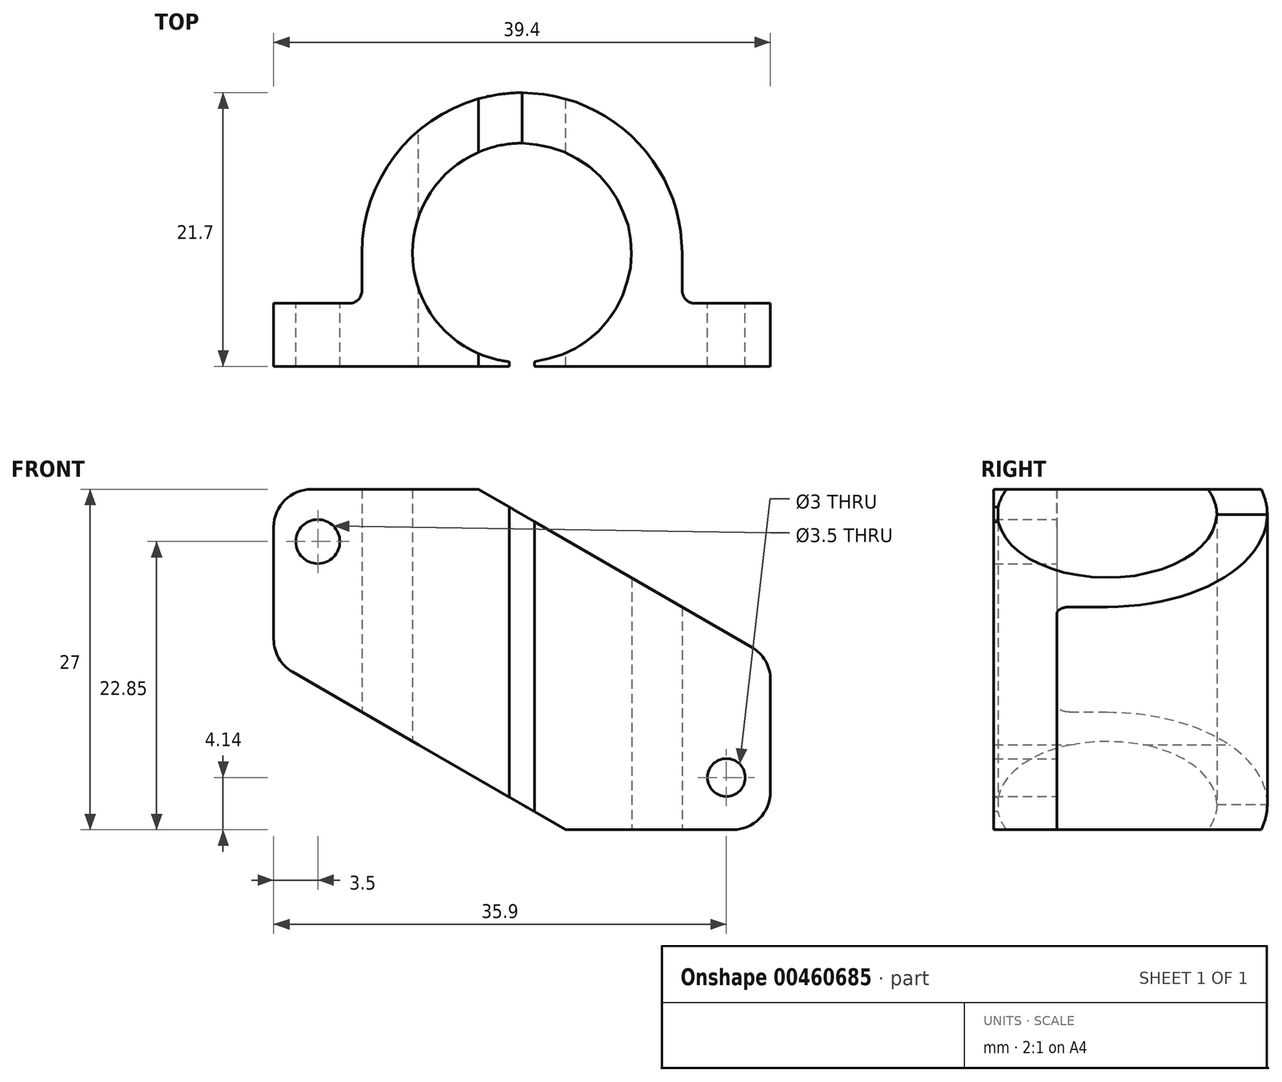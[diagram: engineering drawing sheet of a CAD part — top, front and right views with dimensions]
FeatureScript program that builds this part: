
annotation { "Feature Type Name" : "Feature", "Feature Type Description" : "" }
export const myFeature = defineFeature(function(context is Context, id is Id, definition is map)
    precondition{}
    {
        {
            var Q0;
            Q0=qCreatedBy(makeId("Top.planeOp"),FACE);
            var sketch = newSketch(context, id + "F0", { "sketchPlane" : qUnion([Q0])});
            skCircle(sketch, "E0", {"center": v(0, 0) * mm, "radius": 8.7 * mm});
            skCircle(sketch, "E1", {"center": v(0, 0) * mm, "radius": 12.7 * mm});
            skLineSegment(sketch, "E2.bottom", {"start": v(-12.7, 0) * mm, "end": v(12.7, 0) * mm});
            skLineSegment(sketch, "E2.top", {"start": v(-12.7, -9) * mm, "end": v(12.7, -9) * mm});
            skLineSegment(sketch, "E2.left", {"start": v(-12.7, 0) * mm, "end": v(-12.7, -9) * mm});
            skLineSegment(sketch, "E2.right", {"start": v(12.7, 0) * mm, "end": v(12.7, -9) * mm});
            skLineSegment(sketch, "E3.bottom", {"start": v(-19.7, -9) * mm, "end": v(19.7, -9) * mm});
            skLineSegment(sketch, "E3.top", {"start": v(-19.7, -4) * mm, "end": v(19.7, -4) * mm});
            skLineSegment(sketch, "E3.left", {"start": v(-19.7, -9) * mm, "end": v(-19.7, -4) * mm});
            skLineSegment(sketch, "E3.right", {"start": v(19.7, -9) * mm, "end": v(19.7, -4) * mm});
            skLineSegment(sketch, "E4.bottom", {"start": v(-1, -9) * mm, "end": v(1, -9) * mm});
            skLineSegment(sketch, "E4.top", {"start": v(-1, -4) * mm, "end": v(1, -4) * mm});
            skLineSegment(sketch, "E4.left", {"start": v(-1, -9) * mm, "end": v(-1, -4) * mm});
            skLineSegment(sketch, "E4.right", {"start": v(1, -9) * mm, "end": v(1, -4) * mm});
            skSolve(sketch);
        }
        {
            var Q0;
            {var subQ5=sQuery(id+"F0.wireOp",EDGE,"E3.left");Q0=makeQuery(id+"F0.imprint","IMPRINT",FACE,{"disambiguationData":[TD([[makeQuery(id+"F0.imprint","IMPRINT",EDGE,{"derivedFrom":subQ5}),-1.0]])]});}
            var Q1;
            {var subQ5=sQuery(id+"F0.wireOp",EDGE,"E3.right");Q1=makeQuery(id+"F0.imprint","IMPRINT",FACE,{"disambiguationData":[TD([[makeQuery(id+"F0.imprint","IMPRINT",EDGE,{"derivedFrom":subQ5}),1.0]])]});}
            var Q2;
            {var subQ0=sQuery(id+"F0.wireOp",EDGE,"E2.left");var subQ3=sQuery(id+"F0.wireOp",EDGE,"E3.top");var subQ5=makeQuery(id+"F0.imprint","INTERSECT",VERTEX,{"derivedFrom":[subQ0,subQ3]});Q2=makeQuery(id+"F0.imprint","IMPRINT",FACE,{"disambiguationData":[TD([[makeQuery(id+"F0.imprint","IMPRINT",EDGE,{"disambiguationData":[TD([[subQ5,-1.0]])],"derivedFrom":subQ3}),1.0]])]});}
            var Q3;
            {var subQ0=sQuery(id+"F0.wireOp",EDGE,"E2.right");var subQ3=sQuery(id+"F0.wireOp",EDGE,"E3.top");var subQ5=makeQuery(id+"F0.imprint","INTERSECT",VERTEX,{"derivedFrom":[subQ0,subQ3]});Q3=makeQuery(id+"F0.imprint","IMPRINT",FACE,{"disambiguationData":[TD([[makeQuery(id+"F0.imprint","IMPRINT",EDGE,{"disambiguationData":[TD([[subQ5,1.0]])],"derivedFrom":subQ3}),1.0]])]});}
            var Q4;
            {var subQ0=sQuery(id+"F0.wireOp",EDGE,"E2.bottom");var subQ1=sQuery(id+"F0.wireOp",EDGE,"E0");var subQ2=makeQuery(id+"F0.imprint","INTERSECT",VERTEX,{"disambiguationData":[OD(0.0)],"derivedFrom":[subQ1,subQ0]});Q4=makeQuery(id+"F0.imprint","IMPRINT",FACE,{"disambiguationData":[TD([[makeQuery(id+"F0.imprint","IMPRINT",EDGE,{"disambiguationData":[TD([[subQ2,1.0]])],"derivedFrom":subQ1}),-1.0]])]});}
            var Q5;
            {var subQ0=sQuery(id+"F0.wireOp",EDGE,"E2.top");var subQ1=sQuery(id+"F0.wireOp",EDGE,"E1");var subQ2=makeQuery(id+"F0.imprint","INTERSECT",VERTEX,{"disambiguationData":[OD(0.0)],"derivedFrom":[subQ1,subQ0]});Q5=makeQuery(id+"F0.imprint","IMPRINT",FACE,{"disambiguationData":[TD([[makeQuery(id+"F0.imprint","IMPRINT",EDGE,{"disambiguationData":[TD([[subQ2,1.0]])],"derivedFrom":subQ1}),-1.0]])]});}
            var Q6;
            {var subQ0=sQuery(id+"F0.wireOp",EDGE,"E2.top");var subQ1=sQuery(id+"F0.wireOp",EDGE,"E1");var subQ2=makeQuery(id+"F0.imprint","INTERSECT",VERTEX,{"disambiguationData":[OD(1.0)],"derivedFrom":[subQ1,subQ0]});Q6=makeQuery(id+"F0.imprint","IMPRINT",FACE,{"disambiguationData":[TD([[makeQuery(id+"F0.imprint","IMPRINT",EDGE,{"disambiguationData":[TD([[subQ2,-1.0]])],"derivedFrom":subQ1}),-1.0]])]});}
            var Q7;
            {var subQ0=sQuery(id+"F0.wireOp",EDGE,"E2.bottom");var subQ1=sQuery(id+"F0.wireOp",EDGE,"E0");var subQ2=makeQuery(id+"F0.imprint","INTERSECT",VERTEX,{"disambiguationData":[OD(0.0)],"derivedFrom":[subQ1,subQ0]});Q7=makeQuery(id+"F0.imprint","IMPRINT",FACE,{"disambiguationData":[TD([[makeQuery(id+"F0.imprint","IMPRINT",EDGE,{"disambiguationData":[TD([[subQ2,-1.0]])],"derivedFrom":subQ1}),-1.0]])]});}
            var Q8;
            {var subQ0=sQuery(id+"F0.wireOp",EDGE,"E2.bottom");var subQ1=sQuery(id+"F0.wireOp",EDGE,"E0");var subQ2=makeQuery(id+"F0.imprint","INTERSECT",VERTEX,{"disambiguationData":[OD(1.0)],"derivedFrom":[subQ1,subQ0]});Q8=makeQuery(id+"F0.imprint","IMPRINT",FACE,{"disambiguationData":[TD([[makeQuery(id+"F0.imprint","IMPRINT",EDGE,{"disambiguationData":[TD([[subQ2,1.0]])],"derivedFrom":subQ1}),-1.0]])]});}
            var Q9;
            {var subQ1=sQuery(id+"F0.wireOp",EDGE,"E0");var subQ7=sQuery(id+"F0.wireOp",EDGE,"E4.left");var subQ9=makeQuery(id+"F0.imprint","INTERSECT",VERTEX,{"derivedFrom":[subQ1,subQ7]});Q9=makeQuery(id+"F0.imprint","IMPRINT",FACE,{"disambiguationData":[TD([[makeQuery(id+"F0.imprint","IMPRINT",EDGE,{"disambiguationData":[TD([[subQ9,1.0]])],"derivedFrom":subQ1}),-1.0]])]});}
            var Q10;
            {var subQ1=sQuery(id+"F0.wireOp",EDGE,"E0");var subQ5=sQuery(id+"F0.wireOp",EDGE,"E4.right");var subQ9=makeQuery(id+"F0.imprint","INTERSECT",VERTEX,{"derivedFrom":[subQ1,subQ5]});Q10=makeQuery(id+"F0.imprint","IMPRINT",FACE,{"disambiguationData":[TD([[makeQuery(id+"F0.imprint","IMPRINT",EDGE,{"disambiguationData":[TD([[subQ9,-1.0]])],"derivedFrom":subQ1}),-1.0]])]});}
            extrude(context, id + "F1", {"entities" : qUnion([Q0, Q1, Q2, Q3, Q4, Q5, Q6, Q7, Q8, Q9, Q10]), "depth" : 25 * mm, "offsetDistance" : 25 * mm, "hasSecondDirection" : true, "secondDirectionOppositeDirection" : true, "secondDirectionDepth" : 2 * mm});
        }
        {
            var Q0;
            Q0=qCreatedBy(makeId("Front.planeOp"),FACE);
            var sketch = newSketch(context, id + "F2", { "sketchPlane" : qUnion([Q0])});
            skLineSegment(sketch, "E5", {"start": v(0, 0) * mm, "end": v(-8.2, 0) * mm});
            skLineSegment(sketch, "E6", {"start": v(-8.2, 0) * mm, "end": v(-8.2, 4.74) * mm});
            skLineSegment(sketch, "E7", {"start": v(-8.2, 4.74) * mm, "end": v(0, 0) * mm});
            skLineSegment(sketch, "E8", {"start": v(-21.54, 12.43) * mm, "end": v(-21.54, -2) * mm});
            skLineSegment(sketch, "E9", {"start": v(-21.54, -2) * mm, "end": v(3.46, -2) * mm});
            skLineSegment(sketch, "E10", {"start": v(3.46, -2) * mm, "end": v(-21.54, 12.43) * mm});
            skSolve(sketch);
        }
        {
            var Q0;
            Q0=qCreatedBy(makeId("Front.planeOp"),FACE);
            var sketch = newSketch(context, id + "F3", { "sketchPlane" : qUnion([Q0])});
            skLineSegment(sketch, "E11", {"start": v(0, 23) * mm, "end": v(39.84, 0) * mm});
            skLineSegment(sketch, "E12", {"start": v(39.84, 0) * mm, "end": v(39.84, 23) * mm});
            skLineSegment(sketch, "E13", {"start": v(39.84, 23) * mm, "end": v(0, 23) * mm});
            skLineSegment(sketch, "E14", {"start": v(29, 6.26) * mm, "end": v(29, 25) * mm});
            skLineSegment(sketch, "E15", {"start": v(29, 25) * mm, "end": v(-3.46, 25) * mm});
            skLineSegment(sketch, "E16", {"start": v(-3.46, 25) * mm, "end": v(29, 6.26) * mm});
            skSolve(sketch);
        }
        {
            var Q0;
            Q0=qSketchRegion(id+"F3",true);
            extrude(context, id + "F4", {"entities" : qUnion([Q0]), "operationType" : NewBodyOperationType.REMOVE, "depth" : 25 * mm, "offsetDistance" : 25 * mm, "hasSecondDirection" : true, "secondDirectionOppositeDirection" : true, "secondDirectionDepth" : 25 * mm});
        }
        {
            var Q0;
            Q0=qSketchRegion(id+"F2",true);
            extrude(context, id + "F5", {"entities" : qUnion([Q0]), "operationType" : NewBodyOperationType.REMOVE, "depth" : 25 * mm, "offsetDistance" : 25 * mm, "hasSecondDirection" : true, "secondDirectionOppositeDirection" : true, "secondDirectionDepth" : 25 * mm});
        }
        {
            var Q0;
            Q0=makeQuery(id+"F1.opExtrude","SWEPT_EDGE",EDGE,{"disambiguationData":[OSD([sQuery(id+"F0.wireOp",EDGE,"E2.right"),sQuery(id+"F0.wireOp",EDGE,"E3.top")])]});
            var Q1;
            Q1=makeQuery(id+"F1.opExtrude","SWEPT_EDGE",EDGE,{"disambiguationData":[OSD([sQuery(id+"F0.wireOp",EDGE,"E2.left"),sQuery(id+"F0.wireOp",EDGE,"E3.top")])]});
            fillet(context, id + "F6", {"entities" : qUnion([Q0, Q1]), "radius" : 1 * mm, "tangentPropagation" : true, "allowEdgeOverflow" : false});
        }
        {
            var Q0;
            Q0=qCreatedBy(makeId("Front.planeOp"),FACE);
            var sketch = newSketch(context, id + "F7", { "sketchPlane" : qUnion([Q0])});
            skCircle(sketch, "E17", {"center": v(-16.2, 20.85) * mm, "radius": 1.75 * mm});
            skCircle(sketch, "E18", {"center": v(16.2, 2.14) * mm, "radius": 1.5 * mm});
            skSolve(sketch);
        }
        {
            var Q0;
            Q0=qSketchRegion(id+"F7",true);
            extrude(context, id + "F8", {"entities" : qUnion([Q0]), "operationType" : NewBodyOperationType.REMOVE, "depth" : 25 * mm, "offsetDistance" : 25 * mm});
        }
        {
            var Q0;
            Q0=makeQuery(id+"F1.opExtrude","CAP_EDGE",EDGE,{"disambiguationData":[OSD([sQuery(id+"F0.wireOp",EDGE,"E3.right")])],"isStart":true});
            var Q1;
            Q1=makeQuery(id+"F4.boolean.opBoolean","INTERSECT",EDGE,{"derivedFrom":[makeQuery(id+"F1.opExtrude","SWEPT_FACE",FACE,{"disambiguationData":[OSD([sQuery(id+"F0.wireOp",EDGE,"E3.right")])]}),makeQuery(id+"F4.opExtrude","SWEPT_FACE",FACE,{"disambiguationData":[OSD([sQuery(id+"F3.wireOp",EDGE,"E11")])]})]});
            var Q2;
            Q2=makeQuery(id+"F1.opExtrude","CAP_EDGE",EDGE,{"disambiguationData":[OSD([sQuery(id+"F0.wireOp",EDGE,"E3.left")])],"isStart":false});
            var Q3;
            {var subQ0=sQuery(id+"F2.wireOp",EDGE,"E10");Q3=makeQuery(id+"F5.boolean.opBoolean","INTERSECT",EDGE,{"derivedFrom":[makeQuery(id+"F1.opExtrude","SWEPT_FACE",FACE,{"disambiguationData":[OSD([sQuery(id+"F0.wireOp",EDGE,"E3.left")])]}),makeQuery(id+"F5.opExtrude","SWEPT_FACE",FACE,{"disambiguationData":[OSD([subQ0]),TDD([makeQuery(id+"F2.imprint","IMPRINT",EDGE,{"disambiguationData":[TD([[makeQuery(id+"F2.imprint","INTERSECT",VERTEX,{"derivedFrom":[sQuery(id+"F2.wireOp",EDGE,"E8"),subQ0]}),1.0]])],"derivedFrom":subQ0})])]})]});}
            var Q4;
            {var subQ1=sQuery(id+"F0.wireOp",EDGE,"E1");var subQ2=sQuery(id+"F3.wireOp",EDGE,"E16");Q4=makeQuery(id+"F4.boolean.opBoolean","COPY",EDGE,{"disambiguationData":[TD([makeQuery(id+"F1.opExtrude","SWEPT_FACE",FACE,{"disambiguationData":[OSD([subQ1])]})])],"derivedFrom":makeQuery(id+"F4.opExtrude","SWEPT_EDGE",EDGE,{"disambiguationData":[OSD([sQuery(id+"F3.wireOp",EDGE,"E15"),subQ2])]})});}
            var Q5;
            {var subQ1=sQuery(id+"F2.wireOp",EDGE,"E10");var subQ2=sQuery(id+"F2.wireOp",EDGE,"E9");var subQ3=sQuery(id+"F0.wireOp",EDGE,"E1");Q5=makeQuery(id+"F5.boolean.opBoolean","COPY",EDGE,{"disambiguationData":[TD([makeQuery(id+"F1.opExtrude","SWEPT_FACE",FACE,{"disambiguationData":[OSD([subQ3])]})])],"derivedFrom":makeQuery(id+"F5.opExtrude","SWEPT_EDGE",EDGE,{"disambiguationData":[OSD([subQ2,subQ1])]})});}
            var Q6;
            {var subQ1=sQuery(id+"F2.wireOp",EDGE,"E10");var subQ2=sQuery(id+"F2.wireOp",EDGE,"E9");var subQ3=sQuery(id+"F0.wireOp",EDGE,"E4.right");var subQ4=sQuery(id+"F0.wireOp",EDGE,"E3.right");var subQ5=sQuery(id+"F0.wireOp",EDGE,"E3.bottom");var subQ7=sQuery(id+"F0.wireOp",EDGE,"E2.top");var subQ8=sQuery(id+"F0.wireOp",EDGE,"E1");var subQ10=makeQuery(id+"F0.imprint","INTERSECT",VERTEX,{"disambiguationData":[OD(1.0)],"derivedFrom":[subQ8,subQ7]});Q6=makeQuery(id+"F5.boolean.opBoolean","COPY",EDGE,{"disambiguationData":[TD([makeQuery(id+"F1.opExtrude","SWEPT_FACE",FACE,{"disambiguationData":[OSD([subQ7,subQ5]),TDD([makeQuery(id+"F0.imprint","IMPRINT",EDGE,{"disambiguationData":[TD([[makeQuery(id+"F0.imprint","INTERSECT",VERTEX,{"derivedFrom":[subQ7,subQ3]}),-1.0]])],"derivedFrom":subQ7}),makeQuery(id+"F0.imprint","IMPRINT",EDGE,{"disambiguationData":[TD([[subQ10,-1.0]])],"derivedFrom":subQ7}),makeQuery(id+"F0.imprint","IMPRINT",EDGE,{"disambiguationData":[TD([[makeQuery(id+"F0.imprint","INTERSECT",VERTEX,{"derivedFrom":[subQ5,subQ4]}),1.0]])],"derivedFrom":subQ5})])]})])],"derivedFrom":makeQuery(id+"F5.opExtrude","SWEPT_EDGE",EDGE,{"disambiguationData":[OSD([subQ2,subQ1])]})});}
            var Q7;
            {var subQ1=sQuery(id+"F0.wireOp",EDGE,"E3.bottom");var subQ3=sQuery(id+"F0.wireOp",EDGE,"E2.top");var subQ5=sQuery(id+"F0.wireOp",EDGE,"E3.left");var subQ6=sQuery(id+"F0.wireOp",EDGE,"E1");var subQ7=makeQuery(id+"F0.imprint","INTERSECT",VERTEX,{"disambiguationData":[OD(0.0)],"derivedFrom":[subQ6,subQ3]});var subQ9=sQuery(id+"F3.wireOp",EDGE,"E16");Q7=makeQuery(id+"F4.boolean.opBoolean","COPY",EDGE,{"disambiguationData":[TD([makeQuery(id+"F1.opExtrude","SWEPT_FACE",FACE,{"disambiguationData":[OSD([subQ3,subQ1]),TDD([makeQuery(id+"F0.imprint","IMPRINT",EDGE,{"disambiguationData":[TD([[subQ7,-1.0]])],"derivedFrom":subQ3}),makeQuery(id+"F0.imprint","IMPRINT",EDGE,{"disambiguationData":[TD([[subQ7,1.0]])],"derivedFrom":subQ3}),makeQuery(id+"F0.imprint","IMPRINT",EDGE,{"disambiguationData":[TD([[makeQuery(id+"F0.imprint","INTERSECT",VERTEX,{"derivedFrom":[subQ1,subQ5]}),-1.0]])],"derivedFrom":subQ1})])]})])],"derivedFrom":makeQuery(id+"F4.opExtrude","SWEPT_EDGE",EDGE,{"disambiguationData":[OSD([sQuery(id+"F3.wireOp",EDGE,"E15"),subQ9])]})});}
            fillet(context, id + "F9", {"entities" : qUnion([Q0, Q1, Q2, Q3, Q4, Q5, Q6, Q7]), "radius" : 3 * mm, "tangentPropagation" : true, "allowEdgeOverflow" : false});
        }
    });
